# Revit family: EU_SINGLE_IDU_360_CST_S_Ver.1.0
name_source: partatom
category: Mechanical Equipment
revit_build: Autodesk Revit 2016 (Build: 20150220_1215(x64)
units: mm (PartAtom-declared; Revit-internal decimal feet)

## family parameters
Always vertical = Yes
Cut with Voids When Loaded = No
OmniClass Number = 23.75.00.00
OmniClass Title = Climate Control (HVAC)
Part Type = Normal
Room Calculation Point = No
Round Connector Dimension = Use Diameter
Shared = No
Work Plane-Based = No

## types (3) — shared parameters
Designation = -
Free Content Downloads = -
Location = -
Manufacturer = SAMSUNG
Manufacturer Metadata = -
Net Weight = 20.20 kg
Notes = -
Product Documentation Link = -
Product Page URL = -
Sales Rep Locator = -
Serial Number = -
Subscribe for Update Alerts = -
System Served = -
URL = www.samsung.com

## per-type parameters (varying)
| type | Circle | Model | Panel Model | Panel Net Weigh | Refrigerant Type | Square |
| 7.10 kW,  220-240V, 360 CASSETTE (Circle) | Yes | AC071MN4PKH/EU | PC4NUNMAN | 2.70 kg | R410A | No |
| 7.10 kW,  220-240V, 360 CASSETTE (Square) | No | AC071MN4PKH/EU | PC4NUDMAN | 3.60 kg | R410A | Yes |
| 7.1kW, 220-240V, 360 CASSETTE, R32 | Yes | AC071RN4PKG/EU | PC4NUDMAN | 3.60 kg | R32 | No |

## geometry (parser evidence)
native form markers: Sweep x9
no freeform markers — native parametric forms only
